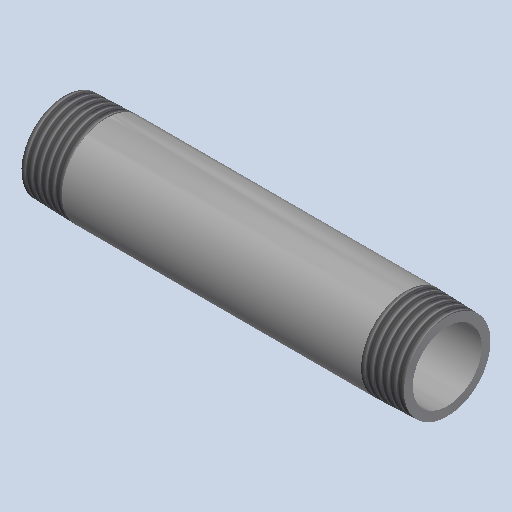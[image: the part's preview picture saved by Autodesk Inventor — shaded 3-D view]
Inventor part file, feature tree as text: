
AUTODESK INVENTOR PART (.ipt)
format: ipt  version: 2025 (Build 290162000, 162)  size: 218,624 bytes
history: native  units: mm (DEFAULTED — no unit token found)
features: other x8, revolve x1
ambient origin geometry x8: Origin, YZ Plane, XZ Plane, XY Plane, X Axis, Y Axis, Z Axis, Center Point
bodies: Solid1 (feature_tree)
feature tree (9):
  revolve  "Revolution1"  [1 undecoded]
  other  "Work Axis1"
  other  "Work Point5"
  other  "Work Axis2"
  other  "Work Point6"
  other  "Work Axis3"
  other  "Work Axis4"
  other  "Work Point7"
  other  "Work Point8"
note: 1 required parameter value undecoded (feature->parameter linkage not recoverable at this tier; creation-order binding heuristic only, values carry confidence <= 0.55)
